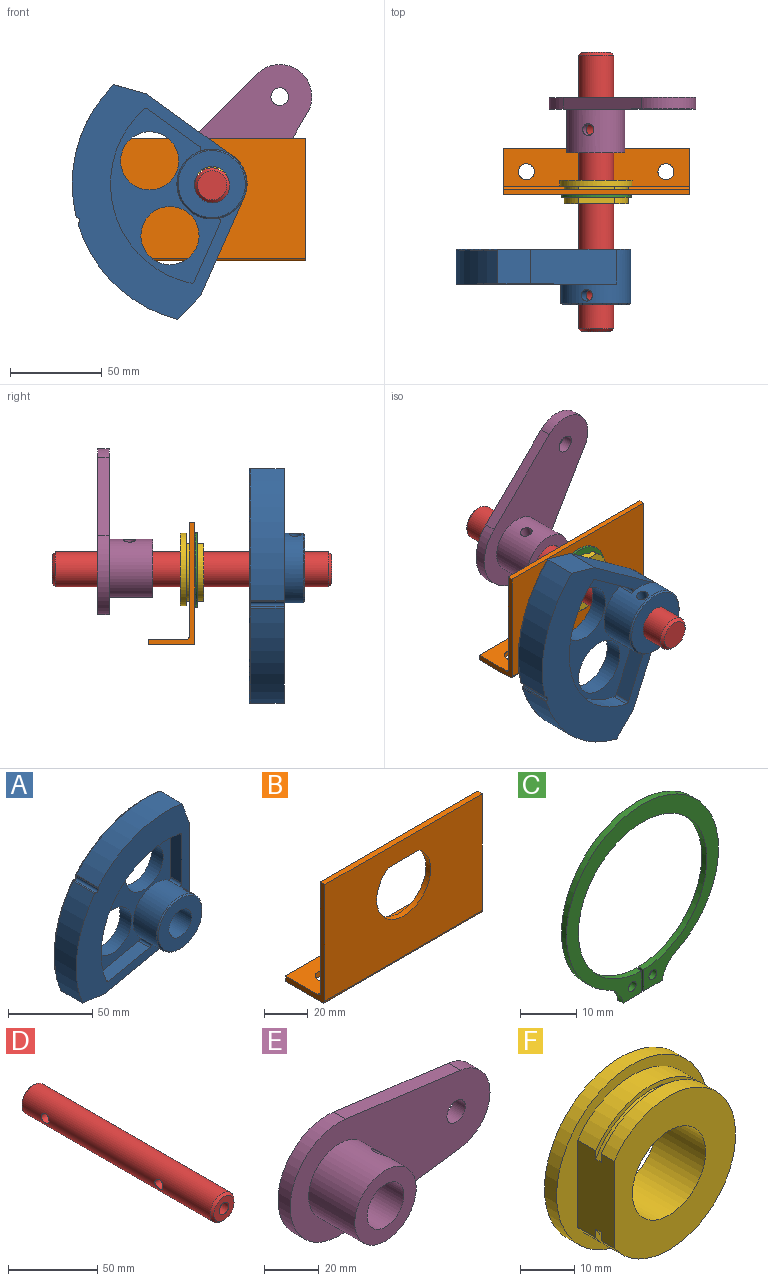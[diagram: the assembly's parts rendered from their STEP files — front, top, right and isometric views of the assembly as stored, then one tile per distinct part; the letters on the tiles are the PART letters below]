
ASSEMBLY  parts=6 mates=5
PART A: 32 faces, bbox 101.5x30.2x113.3 mm
  f0: cylinder r=19.05mm len=38.1mm, axis (0,1,0), area 2201.4mm2, adj f4,f5,f11,f19,f20,f21,f22,f24
  f1: cylinder r=9.55mm len=30.23mm, axis (0,1,0), area 1749.4mm2, adj f5,f23,f25,f26
  f2: cylinder r=15.88mm len=31.75mm, axis (0,1,0), area 962.7mm2, adj f4,f5
  f3: cylinder r=15.88mm len=31.75mm, axis (0,1,0), area 962.7mm2, adj f4,f5
  f4: plane 78.66x67.98mm, normal (0,-1,0), area 1755.2mm2, adj f0,f2,f3,f6,f7,f8,f9,f10
  f5: plane 106.07x94.49mm, normal (0,1,0), area 6188.1mm2, adj f0,f1,f2,f3,f11,f12,f18,f19
  f6: plane 34.53x9.4mm, normal (-0.21,0,0.98), area 331.8mm2, adj f4,f8,f20,f22
  f7: plane 35.3x9.4mm, normal (-1,0,0), area 331.8mm2, adj f4,f10,f21,f22
  f8: cylinder r=1.52mm len=9.4mm, axis (0,1,0), area 19.5mm2, adj f4,f6,f9,f22
  f9: cylinder r=55.28mm len=77.76mm, axis (0,1,0), area 1142.4mm2, adj f4,f8,f10,f22
  f10: cylinder r=1.52mm len=9.4mm, axis (0,1,0), area 19.5mm2, adj f4,f7,f9,f22
  f11: plane 57.69x19.05mm, normal (1,0,0), area 1099mm2, adj f0,f5,f12,f22
  f12: plane 19.05x17.44mm, normal (0.94,0,0.34), area 353.5mm2, adj f5,f11,f13,f22,f27
  f13: cylinder r=76.2mm len=70.53mm, axis (0,1,0), area 1434.2mm2, adj f12,f14,f22,f27
  f14: cylinder r=0.76mm len=18.29mm, axis (0,1,0), area 17.4mm2, adj f13,f15,f22,f28
  f15: cylinder r=1.52mm len=18.29mm, axis (0,1,0), area 67.8mm2, adj f14,f16,f22,f29
  f16: cylinder r=0.76mm len=18.29mm, axis (0,1,0), area 17.4mm2, adj f15,f17,f22,f30
  f17: cylinder r=76.2mm len=74.3mm, axis (0,1,0), area 1434.2mm2, adj f16,f18,f22,f31
  f18: plane 19.05x18.38mm, normal (-0.14,0,-0.99), area 353.5mm2, adj f5,f17,f19,f22,f31
  f19: plane 56.43x19.05mm, normal (0.21,0,-0.98), area 1099mm2, adj f0,f5,f18,f22
  f20: cylinder r=1.52mm len=9.4mm, axis (0,1,0), area 30.7mm2, adj f0,f4,f6,f22
  f21: cylinder r=1.52mm len=9.4mm, axis (0,1,0), area 30.7mm2, adj f0,f4,f7,f22
  f22: plane 106.83x95.25mm, normal (0,-1,0), area 3702.8mm2, adj f0,f6,f7,f8,f9,f10,f11,f12
  f23: plane 36.58x36.58mm, normal (0,-1,0), area 764.2mm2, adj f1,f24
  f24: cone r=18.29mm half-angle=45deg, axis (0,1,0), area 126.4mm2, adj f0,f23
  f25: cylinder r=3.17mm len=11.8mm, axis (-0.63,0,-0.78), area 192.2mm2, adj f0,f1
  f26: cylinder r=3.17mm len=11.8mm, axis (-0.63,0,-0.78), area 192.2mm2, adj f0,f1
  f27: torus R=75.44mm, axis (0,-1,0), area 93.7mm2, adj f5,f12,f13,f28
  f28: sphere r=0.76mm, area 0.7mm2, adj f14,f27,f29
  f29: torus R=2.29mm, axis (0,-1,0), area 5.2mm2, adj f5,f15,f28,f30
  f30: sphere r=0.76mm, area 0.7mm2, adj f16,f29,f31
  f31: torus R=75.44mm, axis (0,-1,0), area 93.7mm2, adj f5,f17,f18,f30
PART B: 14 faces, bbox 101.6x25.4x66.7 mm
  f0: plane 101.6x65.15mm, normal (0,-1,0), area 5707.7mm2, adj f5,f6,f7,f9,f10,f11
  f1: plane 101.6x23.88mm, normal (0,0,-1), area 2306.6mm2, adj f2,f6,f7,f9,f12,f13
  f2: plane 101.6x3.04mm, normal (0,1,0), area 308.6mm2, adj f1,f3,f6,f7
  f3: plane 101.6x20.84mm, normal (0,0,1), area 1997.9mm2, adj f2,f6,f7,f8,f12,f13
  f4: plane 101.6x62.11mm, normal (0,1,0), area 5399mm2, adj f5,f6,f7,f8,f10,f11
  f5: plane 101.6x3.04mm, normal (0,0,1), area 308.6mm2, adj f0,f4,f6,f7
  f6: plane 66.68x25.4mm, normal (-1,0,0), area 270.5mm2, adj f0,f1,f2,f3,f4,f5,f8,f9
  f7: plane 66.68x25.4mm, normal (1,0,0), area 270.5mm2, adj f0,f1,f2,f3,f4,f5,f8,f9
  f8: cylinder r=1.52mm len=101.6mm, axis (1,0,0), area 243.2mm2, adj f3,f4,f6,f7
  f9: cylinder r=1.52mm len=101.6mm, axis (-1,0,0), area 243.2mm2, adj f0,f1,f6,f7
  f10: plane 19.68x3.04mm, normal (0,0,-1), area 59.8mm2, adj f0,f4,f11
  f11: cylinder r=17.41mm len=34.82mm, axis (0,-1,0), area 268.8mm2, adj f0,f4,f10
  f12: cylinder r=4.36mm len=8.71mm, axis (0,0,1), area 83.1mm2, adj f1,f3
  f13: cylinder r=4.36mm len=8.71mm, axis (0,0,1), area 83.1mm2, adj f1,f3
PART C: 12 faces, bbox 38.3x1.3x40.8 mm
  f0: cylinder r=19.13mm len=38.25mm, axis (0,1,0), area 131.2mm2, adj f1,f8,f10,f11
  f1: cylinder r=6.34mm len=4.3mm, axis (0,1,0), area 6.9mm2, adj f0,f2,f10,f11
  f2: plane 4.67x1.27mm, normal (0,0,-1), area 5.9mm2, adj f1,f3,f10,f11
  f3: plane 4.68x1.27mm, normal (1,0,0), area 5.9mm2, adj f2,f4,f10,f11
  f4: cylinder r=16.15mm len=32.31mm, axis (0,1,0), area 128.3mm2, adj f3,f5,f10,f11
  f5: plane 4.68x1.27mm, normal (-1,0,0), area 5.9mm2, adj f4,f6,f10,f11
  f6: plane 4.67x1.27mm, normal (0,0,-1), area 5.9mm2, adj f5,f8,f10,f11
  f7: cylinder r=0.99mm len=1.98mm, axis (0,1,0), area 7.9mm2, adj f10,f11
  f8: cylinder r=6.34mm len=4.54mm, axis (0,1,0), area 7.5mm2, adj f0,f6,f10,f11
  f9: cylinder r=0.99mm len=1.98mm, axis (0,1,0), area 7.9mm2, adj f10,f11
  f10: plane 40.84x38.25mm, normal (0,-1,0), area 354mm2, adj f0,f1,f2,f3,f4,f5,f6,f7
  f11: plane 40.84x38.25mm, normal (0,1,0), area 354mm2, adj f0,f1,f2,f3,f4,f5,f6,f7
PART D: 9 faces, bbox 19.1x152.4x19.1 mm
  f0: cylinder r=9.53mm len=149.35mm, axis (0,1,0), area 8809.5mm2, adj f3,f4,f5,f6
  f1: plane 16x16mm, normal (0,1,0), area 201.1mm2, adj f3
  f2: plane 16x16mm, normal (0,-1,0), area 153.4mm2, adj f4,f8
  f3: cone r=8mm half-angle=45deg, axis (0,-1,0), area 118.7mm2, adj f0,f1
  f4: cone r=9.53mm half-angle=45deg, axis (0,1,0), area 118.7mm2, adj f0,f2
  f5: cylinder r=3.17mm len=19.05mm, axis (1,0,0), area 369.3mm2, adj f0
  f6: cylinder r=3.17mm len=19.05mm, axis (1,0,0), area 369.3mm2, adj f0
  f7: cone r=0mm half-angle=59deg, axis (0,-1,0), area 55.7mm2, adj f8
  f8: cylinder r=3.9mm len=19.05mm, axis (0,-1,0), area 466.7mm2, adj f2,f7
PART E: 14 faces, bbox 103.4x30.2x50.8 mm
  f0: cylinder r=25.4mm len=50.8mm, axis (0,1,0), area 548.8mm2, adj f1,f3,f6,f7
  f1: plane 59.43x7.81mm, normal (0.13,0,-0.99), area 380.6mm2, adj f0,f2,f6,f7
  f2: cylinder r=17.53mm len=34.75mm, axis (0,1,0), area 320.6mm2, adj f1,f3,f6,f7
  f3: plane 59.43x7.81mm, normal (0.13,0,0.99), area 380.6mm2, adj f0,f2,f6,f7
  f4: cylinder r=12.89mm len=25.78mm, axis (0,1,0), area 514.3mm2, adj f7,f11
  f5: cylinder r=4.79mm len=9.58mm, axis (0,1,0), area 191mm2, adj f6,f7
  f6: plane 103.38x50.8mm, normal (0,-1,0), area 3249.2mm2, adj f0,f1,f2,f3,f5,f9
  f7: plane 103.38x50.8mm, normal (0,1,0), area 3518.9mm2, adj f0,f1,f2,f3,f4,f5
  f8: cylinder r=9.55mm len=23.88mm, axis (0,1,0), area 1368.5mm2, adj f10,f11,f12,f13
  f9: cylinder r=15.88mm len=31.75mm, axis (0,1,0), area 2318mm2, adj f6,f10,f12,f13
  f10: plane 31.75x31.75mm, normal (0,-1,0), area 505.2mm2, adj f8,f9
  f11: plane 25.78x25.78mm, normal (0,1,0), area 235.5mm2, adj f4,f8
  f12: cylinder r=3.17mm len=9.31mm, axis (0.6,0,0.8), area 128.3mm2, adj f8,f9
  f13: cylinder r=3.17mm len=9.31mm, axis (0.6,0,0.8), area 128.4mm2, adj f8,f9
PART F: 11 faces, bbox 39.6x12.7x39.6 mm
  f0: cylinder r=9.56mm len=19.13mm, axis (0,1,0), area 763.1mm2, adj f3,f9
  f1: cylinder r=19.81mm len=39.62mm, axis (0,1,0), area 395.2mm2, adj f2,f3
  f2: plane 39.62x39.62mm, normal (0,-1,0), area 322.8mm2, adj f1,f4,f5
  f3: plane 39.62x39.62mm, normal (0,1,0), area 945.8mm2, adj f0,f1
  f4: plane 19.67x9.53mm, normal (-1,0,0), area 182mm2, adj f2,f5,f6,f7,f8,f9,f10
  f5: cylinder r=17.4mm len=34.8mm, axis (0,1,0), area 419.9mm2, adj f2,f4,f6
  f6: plane 34.8x31.75mm, normal (0,-1,0), area 87.7mm2, adj f4,f5,f7
  f7: cylinder r=16.4mm len=32.79mm, axis (0,1,0), area 123mm2, adj f4,f6,f10
  f8: cylinder r=17.4mm len=34.8mm, axis (0,1,0), area 296.4mm2, adj f4,f9,f10
  f9: plane 34.8x31.75mm, normal (0,-1,0), area 623mm2, adj f0,f4,f8
  f10: plane 34.8x31.75mm, normal (0,1,0), area 87.7mm2, adj f4,f7,f8
PLACE A rot(axis=(0,-1,0),54.2deg) t=(1.21,-24.05,34.97)mm
PLACE B t=(1.39,5.67,-6.98)mm fixed
PLACE C t=(1.39,5.54,34.29)mm
PLACE D rot(axis=(0.79,0,-0.61),180deg) t=(1.39,-69.01,34.29)mm
PLACE E rot(axis=(0,-1,0),52.2deg) t=(1.21,58.76,34.95)mm
PLACE F rot(axis=(0,1,0),90deg) t=(1.39,13.54,34.29)mm
MATE cylindrical D.f0 <-> F.f0  axis (0,-1,0) through (1.39,7.19,34.29)mm
MATE fastened E.f12 <-> D.f5  axis (-0.26,0,0.97) through (-1.13,41.23,43.6)mm
MATE slider F.f0 <-> B.f11  axis (0,1,0) through (1.39,7.19,34.29)mm
MATE revolute C.f4 <-> F.f7  axis (0,1,0) through (1.39,4.91,34.29)mm
MATE fastened A.f25 <-> D.f6  axis (0.26,0,-0.97) through (-1.13,-49.19,43.6)mm
